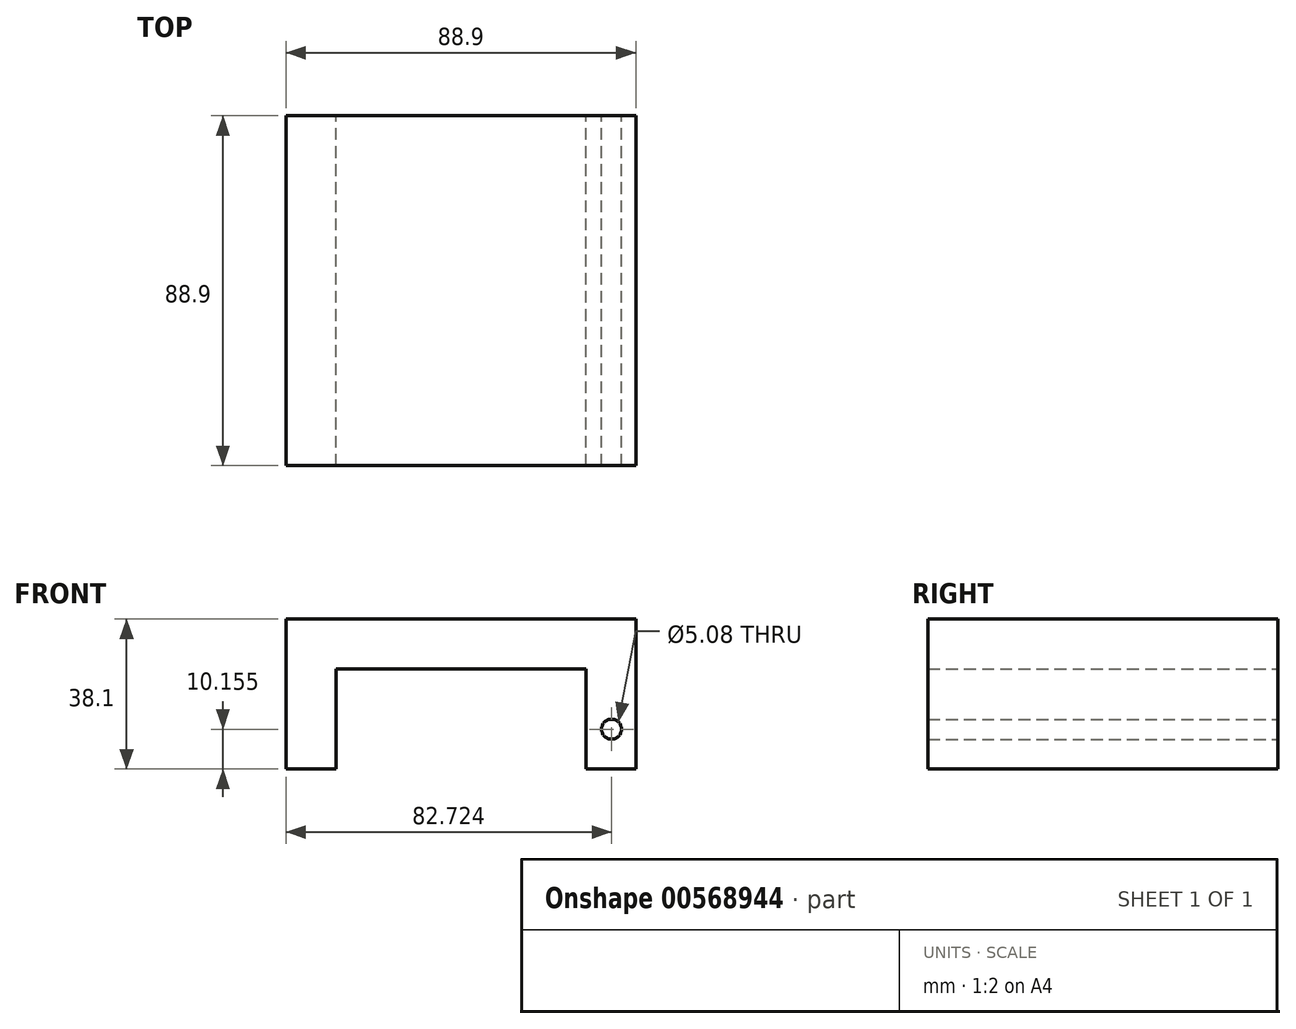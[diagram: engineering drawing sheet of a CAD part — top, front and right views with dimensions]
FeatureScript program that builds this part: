
annotation { "Feature Type Name" : "Feature", "Feature Type Description" : "" }
export const myFeature = defineFeature(function(context is Context, id is Id, definition is map)
    precondition{}
    {
        {
            var Q0;
            Q0=qCreatedBy(makeId("Front.planeOp"),FACE);
            var sketch = newSketch(context, id + "F0", { "sketchPlane" : qUnion([Q0])});
            skLineSegment(sketch, "E0", {"start": v(-76.2, -38.04) * mm, "end": v(-76.2, -12.64) * mm});
            skLineSegment(sketch, "E1", {"start": v(-88.9, -38.04) * mm, "end": v(-88.9, -12.64) * mm});
            skLineSegment(sketch, "E2", {"start": v(-88.9, -12.64) * mm, "end": v(-88.9, 0.06) * mm});
            skLineSegment(sketch, "E3", {"start": v(-88.9, 0.06) * mm, "end": v(0, 0.06) * mm});
            skLineSegment(sketch, "E4", {"start": v(0, 0.06) * mm, "end": v(0, -38.04) * mm});
            skLineSegment(sketch, "E5", {"start": v(0, -38.04) * mm, "end": v(-12.7, -38.04) * mm});
            skLineSegment(sketch, "E6", {"start": v(-12.7, -38.04) * mm, "end": v(-12.7, -12.64) * mm});
            skLineSegment(sketch, "E7", {"start": v(-12.7, -12.64) * mm, "end": v(-76.2, -12.64) * mm});
            skLineSegment(sketch, "E8", {"start": v(-88.9, -38.04) * mm, "end": v(-76.2, -38.04) * mm});
            skCircle(sketch, "E9", {"center": v(-6.18, -27.89) * mm, "radius": 2.54 * mm});
            skPoint(sketch, "E10.center.orphan", {"position": v(-6.18, -18.7) * mm});
            skCircle(sketch, "E11", {"center": v(-59.04, -29.24) * mm, "radius": 2.54 * mm});
            skSolve(sketch);
        }
        {
            var Q0;
            Q0 = qSketchRegion(id + "F0", true);
            extrude(context, id + "F1", {"entities" : qUnion([Q0]), "depth" : 88.9 * mm, "offsetDistance" : 25.4 * mm});
        }
        {
            var Q0;
            Q0=makeQuery(id+"F1.opExtrude","SWEPT_BODY",BODY,{"disambiguationData":[OSD([sQuery(id+"F0.wireOp",EDGE,"E11")])]});
            deleteBodies(context, id + "F2", {"entities" : qUnion([Q0])});
        }
    });
